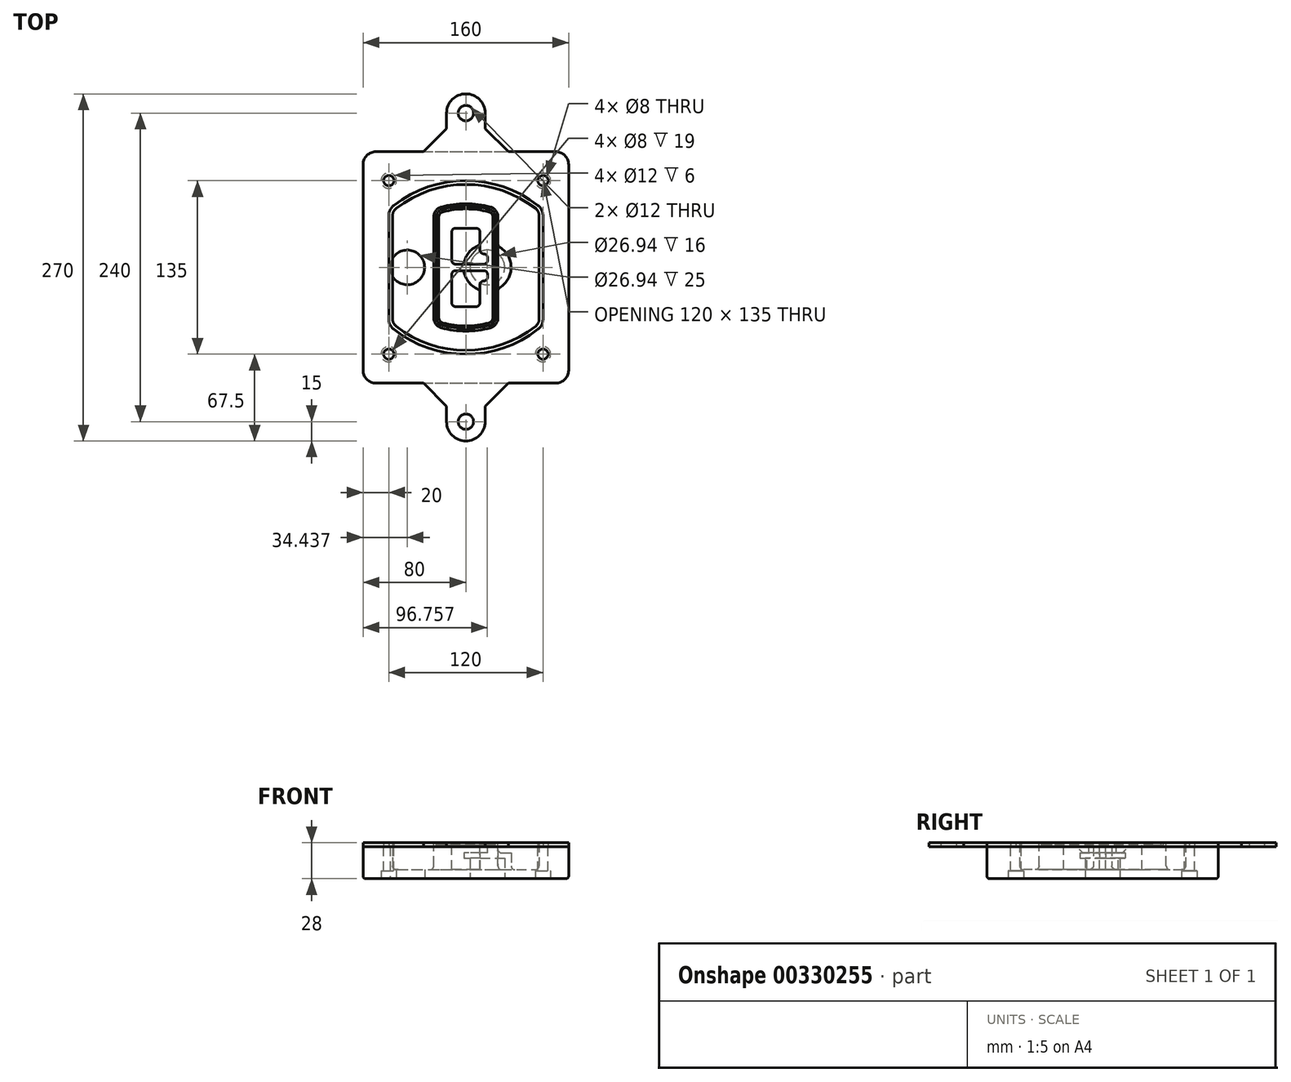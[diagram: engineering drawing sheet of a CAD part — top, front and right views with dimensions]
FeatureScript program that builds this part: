
annotation { "Feature Type Name" : "Feature", "Feature Type Description" : "" }
export const myFeature = defineFeature(function(context is Context, id is Id, definition is map)
    precondition{}
    {
        {
            var Q0;
            Q0=qCreatedBy(makeId("Top.planeOp"),FACE);
            var sketch = newSketch(context, id + "F0", { "sketchPlane" : qUnion([Q0])});
            skPoint(sketch, "E0.rect.middle", {"position": v(0, 0) * mm});
            skLineSegment(sketch, "E1.bottom", {"start": v(-70, -90) * mm, "end": v(70, -90) * mm});
            skLineSegment(sketch, "E1.top", {"start": v(-70, 90) * mm, "end": v(70, 90) * mm});
            skLineSegment(sketch, "E1.left", {"start": v(-80, -80) * mm, "end": v(-80, 80) * mm});
            skLineSegment(sketch, "E1.right", {"start": v(80, -80) * mm, "end": v(80, 80) * mm});
            skLineSegment(sketch, "E2", {"start": v(-80, 90) * mm, "end": v(80, -90) * mm, "construction": true});
            skLineSegment(sketch, "E3", {"start": v(80, 90) * mm, "end": v(-80, -90) * mm, "construction": true});
            skCircle(sketch, "E4", {"center": v(-60, 67.5) * mm, "radius": 4 * mm});
            skCircle(sketch, "E5", {"center": v(60, 67.5) * mm, "radius": 4 * mm});
            skCircle(sketch, "E6", {"center": v(60, -67.5) * mm, "radius": 4 * mm});
            skCircle(sketch, "E7", {"center": v(-60, -67.5) * mm, "radius": 4 * mm});
            skLineSegment(sketch, "E8", {"start": v(-60, 67.5) * mm, "end": v(60, 67.5) * mm, "construction": true});
            skLineSegment(sketch, "E9", {"start": v(60, 67.5) * mm, "end": v(60, -67.5) * mm, "construction": true});
            skLineSegment(sketch, "E10", {"start": v(60, -67.5) * mm, "end": v(-60, -67.5) * mm, "construction": true});
            skLineSegment(sketch, "E11", {"start": v(-60, -67.5) * mm, "end": v(-60, 67.5) * mm, "construction": true});
            skLineSegment(sketch, "E12", {"start": v(-60, 40.3) * mm, "end": v(-60, -40.3) * mm});
            skLineSegment(sketch, "E13", {"start": v(60, 40.3) * mm, "end": v(60, -40.3) * mm});
            skArc(sketch, "E14", {"start": v(56.15, 48.18) * mm, "mid": v(0, 67.5) * mm, "end": v(-56.15, 48.18) * mm});
            skArc(sketch, "E15", {"start": v(-56.15, -48.18) * mm, "mid": v(0, -67.5) * mm, "end": v(56.15, -48.18) * mm});
            skLineSegment(sketch, "E16", {"start": v(-60, 0) * mm, "end": v(60, 0) * mm, "construction": true});
            skPoint(sketch, "E17.visualSharp", {"position": v(-60, -45) * mm});
            skArc(sketch, "E17.filletArc", {"start": v(-60, -40.3) * mm, "mid": v(-58.99, -44.68) * mm, "end": v(-56.15, -48.18) * mm});
            skPoint(sketch, "E18.visualSharp", {"position": v(-60, 45) * mm});
            skArc(sketch, "E18.filletArc", {"start": v(-56.15, 48.18) * mm, "mid": v(-58.99, 44.68) * mm, "end": v(-60, 40.3) * mm});
            skPoint(sketch, "E19.visualSharp", {"position": v(60, 45) * mm});
            skArc(sketch, "E19.filletArc", {"start": v(60, 40.3) * mm, "mid": v(58.99, 44.68) * mm, "end": v(56.15, 48.18) * mm});
            skPoint(sketch, "E20.visualSharp", {"position": v(60, -45) * mm});
            skArc(sketch, "E20.filletArc", {"start": v(56.15, -48.18) * mm, "mid": v(58.99, -44.68) * mm, "end": v(60, -40.3) * mm});
            skPoint(sketch, "E21.visualSharp", {"position": v(-80, 90) * mm});
            skArc(sketch, "E21.filletArc", {"start": v(-70, 90) * mm, "mid": v(-77.07, 87.07) * mm, "end": v(-80, 80) * mm});
            skPoint(sketch, "E22.visualSharp", {"position": v(80, 90) * mm});
            skArc(sketch, "E22.filletArc", {"start": v(80, 80) * mm, "mid": v(77.07, 87.07) * mm, "end": v(70, 90) * mm});
            skPoint(sketch, "E23.visualSharp", {"position": v(80, -90) * mm});
            skArc(sketch, "E23.filletArc", {"start": v(70, -90) * mm, "mid": v(77.07, -87.07) * mm, "end": v(80, -80) * mm});
            skPoint(sketch, "E24.visualSharp", {"position": v(-80, -90) * mm});
            skArc(sketch, "E24.filletArc", {"start": v(-80, -80) * mm, "mid": v(-77.07, -87.07) * mm, "end": v(-70, -90) * mm});
            skArc(sketch, "E25.0", {"start": v(57, 40.3) * mm, "mid": v(56.3, 43.36) * mm, "end": v(54.3, 45.81) * mm});
            skLineSegment(sketch, "E25.1", {"start": v(57, 40.3) * mm, "end": v(57, -40.3) * mm});
            skArc(sketch, "E25.2", {"start": v(54.3, -45.81) * mm, "mid": v(56.3, -43.36) * mm, "end": v(57, -40.3) * mm});
            skArc(sketch, "E25.3", {"start": v(-54.3, -45.81) * mm, "mid": v(0, -64.5) * mm, "end": v(54.3, -45.81) * mm});
            skArc(sketch, "E25.4", {"start": v(-57, -40.3) * mm, "mid": v(-56.3, -43.36) * mm, "end": v(-54.3, -45.81) * mm});
            skArc(sketch, "E25.5", {"start": v(54.3, 45.81) * mm, "mid": v(0, 64.5) * mm, "end": v(-54.3, 45.81) * mm});
            skLineSegment(sketch, "E25.6", {"start": v(-57, 40.3) * mm, "end": v(-57, -40.3) * mm});
            skArc(sketch, "E25.7", {"start": v(-54.3, 45.81) * mm, "mid": v(-56.3, 43.36) * mm, "end": v(-57, 40.3) * mm});
            skArc(sketch, "E26.0", {"start": v(-58.62, 51.33) * mm, "mid": v(-62.58, 46.43) * mm, "end": v(-64, 40.3) * mm});
            skArc(sketch, "E26.1", {"start": v(58.62, 51.33) * mm, "mid": v(0, 71.5) * mm, "end": v(-58.62, 51.33) * mm});
            skArc(sketch, "E26.2", {"start": v(64, 40.3) * mm, "mid": v(62.58, 46.43) * mm, "end": v(58.62, 51.33) * mm});
            skLineSegment(sketch, "E26.3", {"start": v(64, 40.3) * mm, "end": v(64, -40.3) * mm});
            skArc(sketch, "E26.4", {"start": v(58.62, -51.33) * mm, "mid": v(62.58, -46.43) * mm, "end": v(64, -40.3) * mm});
            skLineSegment(sketch, "E26.5", {"start": v(-64, 40.3) * mm, "end": v(-64, -40.3) * mm});
            skArc(sketch, "E26.6", {"start": v(-58.62, -51.33) * mm, "mid": v(0, -71.5) * mm, "end": v(58.62, -51.33) * mm});
            skArc(sketch, "E26.7", {"start": v(-64, -40.3) * mm, "mid": v(-62.58, -46.43) * mm, "end": v(-58.62, -51.33) * mm});
            skSolve(sketch);
        }
        {
            var Q0;
            Q0=makeQuery(id+"F0.imprint","IMPRINT",FACE,{"disambiguationData":[TD([[makeQuery(id+"F0.imprint","IMPRINT",EDGE,{"derivedFrom":sQuery(id+"F0.wireOp",EDGE,"E1.bottom")}),1.0]])]});
            var Q1;
            Q1=makeQuery(id+"F0.imprint","IMPRINT",FACE,{"disambiguationData":[TD([[makeQuery(id+"F0.imprint","IMPRINT",EDGE,{"derivedFrom":sQuery(id+"F0.wireOp",EDGE,"E12")}),1.0]])]});
            var Q2;
            Q2=makeQuery(id+"F0.imprint","IMPRINT",FACE,{"disambiguationData":[TD([[makeQuery(id+"F0.imprint","IMPRINT",EDGE,{"derivedFrom":sQuery(id+"F0.wireOp",EDGE,"E25.0")}),1.0]])]});
            var Q3;
            Q3=makeQuery(id+"F0.imprint","IMPRINT",FACE,{"disambiguationData":[TD([[makeQuery(id+"F0.imprint","IMPRINT",EDGE,{"derivedFrom":sQuery(id+"F0.wireOp",EDGE,"E12")}),-1.0]])]});
            extrude(context, id + "F1", {"entities" : qUnion([Q0, Q1, Q2, Q3]), "oppositeDirection" : true, "depth" : 25 * mm});
        }
        {
            var Q0;
            Q0=makeQuery(id+"F0.imprint","IMPRINT",FACE,{"disambiguationData":[TD([[makeQuery(id+"F0.imprint","IMPRINT",EDGE,{"derivedFrom":sQuery(id+"F0.wireOp",EDGE,"E12")}),1.0]])]});
            extrude(context, id + "F2", {"entities" : qUnion([Q0]), "operationType" : NewBodyOperationType.ADD, "depth" : 3 * mm});
        }
        {
            var Q0;
            Q0=makeQuery(id+"F0.imprint","IMPRINT",FACE,{"disambiguationData":[TD([[makeQuery(id+"F0.imprint","IMPRINT",EDGE,{"derivedFrom":sQuery(id+"F0.wireOp",EDGE,"E25.0")}),1.0]])]});
            extrude(context, id + "F3", {"entities" : qUnion([Q0]), "operationType" : NewBodyOperationType.REMOVE, "oppositeDirection" : true, "depth" : 18 * mm});
        }
        {
            var Q0;
            Q0=makeQuery(id+"F2.opExtrude","CAP_FACE",FACE,{"disambiguationData":[OSD([sQuery(id+"F0.wireOp",EDGE,"E12"),sQuery(id+"F0.wireOp",EDGE,"E13"),sQuery(id+"F0.wireOp",EDGE,"E14"),sQuery(id+"F0.wireOp",EDGE,"E15"),sQuery(id+"F0.wireOp",EDGE,"E17.filletArc"),sQuery(id+"F0.wireOp",EDGE,"E18.filletArc"),sQuery(id+"F0.wireOp",EDGE,"E19.filletArc"),sQuery(id+"F0.wireOp",EDGE,"E20.filletArc"),sQuery(id+"F0.wireOp",EDGE,"E25.0"),sQuery(id+"F0.wireOp",EDGE,"E25.1"),sQuery(id+"F0.wireOp",EDGE,"E25.2"),sQuery(id+"F0.wireOp",EDGE,"E25.3"),sQuery(id+"F0.wireOp",EDGE,"E25.4"),sQuery(id+"F0.wireOp",EDGE,"E25.5"),sQuery(id+"F0.wireOp",EDGE,"E25.6"),sQuery(id+"F0.wireOp",EDGE,"E25.7")])],"isStart":false});
            var sketch = newSketch(context, id + "F4", { "sketchPlane" : qUnion([Q0])});
            skArc(sketch, "E27.0", {"start": v(-19.08, -46.97) * mm, "mid": v(0, -49.5) * mm, "end": v(19.08, -46.97) * mm});
            skArc(sketch, "E28.0", {"start": v(19.08, 46.97) * mm, "mid": v(0, 49.5) * mm, "end": v(-19.08, 46.97) * mm});
            skLineSegment(sketch, "E29", {"start": v(-25, 39.25) * mm, "end": v(-25, -39.25) * mm});
            skLineSegment(sketch, "E30", {"start": v(25, 39.25) * mm, "end": v(25, -39.25) * mm});
            skLineSegment(sketch, "E31", {"start": v(-25, 45.1) * mm, "end": v(25, 45.1) * mm, "construction": true});
            skLineSegment(sketch, "E32", {"start": v(-25, -45.1) * mm, "end": v(25, -45.1) * mm, "construction": true});
            skPoint(sketch, "E33.visualSharp", {"position": v(-25, 45.1) * mm});
            skArc(sketch, "E33.filletArc", {"start": v(-19.08, 46.97) * mm, "mid": v(-23.35, 44.11) * mm, "end": v(-25, 39.25) * mm});
            skPoint(sketch, "E34.visualSharp", {"position": v(25, 45.1) * mm});
            skArc(sketch, "E34.filletArc", {"start": v(25, 39.25) * mm, "mid": v(23.35, 44.11) * mm, "end": v(19.08, 46.97) * mm});
            skPoint(sketch, "E35.visualSharp", {"position": v(25, -45.1) * mm});
            skArc(sketch, "E35.filletArc", {"start": v(19.08, -46.97) * mm, "mid": v(23.35, -44.11) * mm, "end": v(25, -39.25) * mm});
            skPoint(sketch, "E36.visualSharp", {"position": v(-25, -45.1) * mm});
            skArc(sketch, "E36.filletArc", {"start": v(-25, -39.25) * mm, "mid": v(-23.35, -44.11) * mm, "end": v(-19.08, -46.97) * mm});
            skArc(sketch, "E37.0", {"start": v(54.3, 45.81) * mm, "mid": v(0, 64.5) * mm, "end": v(-54.3, 45.81) * mm});
            skArc(sketch, "E37.1", {"start": v(-54.3, 45.81) * mm, "mid": v(-56.3, 43.36) * mm, "end": v(-57, 40.3) * mm});
            skLineSegment(sketch, "E37.2", {"start": v(-57, 40.3) * mm, "end": v(-57, -40.3) * mm});
            skArc(sketch, "E37.3", {"start": v(-57, -40.3) * mm, "mid": v(-56.3, -43.36) * mm, "end": v(-54.3, -45.81) * mm});
            skArc(sketch, "E37.4", {"start": v(-54.3, -45.81) * mm, "mid": v(0, -64.5) * mm, "end": v(54.3, -45.81) * mm});
            skArc(sketch, "E37.5", {"start": v(54.3, -45.81) * mm, "mid": v(56.3, -43.36) * mm, "end": v(57, -40.3) * mm});
            skLineSegment(sketch, "E37.6", {"start": v(57, 40.3) * mm, "end": v(57, -40.3) * mm});
            skArc(sketch, "E37.7", {"start": v(57, 40.3) * mm, "mid": v(56.3, 43.36) * mm, "end": v(54.3, 45.81) * mm});
            skLineSegment(sketch, "E38.0", {"start": v(23, 39.25) * mm, "end": v(23, -39.25) * mm});
            skArc(sketch, "E38.1", {"start": v(18.56, -45.04) * mm, "mid": v(21.76, -42.9) * mm, "end": v(23, -39.25) * mm});
            skArc(sketch, "E38.2", {"start": v(-18.56, -45.04) * mm, "mid": v(0, -47.5) * mm, "end": v(18.56, -45.04) * mm});
            skArc(sketch, "E38.3", {"start": v(-23, -39.25) * mm, "mid": v(-21.76, -42.9) * mm, "end": v(-18.56, -45.04) * mm});
            skLineSegment(sketch, "E38.4", {"start": v(-23, 39.25) * mm, "end": v(-23, -39.25) * mm});
            skArc(sketch, "E38.5", {"start": v(23, 39.25) * mm, "mid": v(21.76, 42.9) * mm, "end": v(18.56, 45.04) * mm});
            skArc(sketch, "E38.6", {"start": v(-18.56, 45.04) * mm, "mid": v(-21.76, 42.9) * mm, "end": v(-23, 39.25) * mm});
            skArc(sketch, "E38.7", {"start": v(18.56, 45.04) * mm, "mid": v(0, 47.5) * mm, "end": v(-18.56, 45.04) * mm});
            skArc(sketch, "E39.0", {"start": v(21, 39.25) * mm, "mid": v(20.18, 41.68) * mm, "end": v(18.04, 43.1) * mm});
            skLineSegment(sketch, "E39.1", {"start": v(21, 39.25) * mm, "end": v(21, -39.25) * mm});
            skArc(sketch, "E39.2", {"start": v(18.04, -43.1) * mm, "mid": v(20.18, -41.68) * mm, "end": v(21, -39.25) * mm});
            skArc(sketch, "E39.3", {"start": v(-18.04, -43.1) * mm, "mid": v(0, -45.5) * mm, "end": v(18.04, -43.1) * mm});
            skArc(sketch, "E39.4", {"start": v(-21, -39.25) * mm, "mid": v(-20.18, -41.68) * mm, "end": v(-18.04, -43.1) * mm});
            skArc(sketch, "E39.5", {"start": v(18.04, 43.1) * mm, "mid": v(0, 45.5) * mm, "end": v(-18.04, 43.1) * mm});
            skLineSegment(sketch, "E39.6", {"start": v(-21, 39.25) * mm, "end": v(-21, -39.25) * mm});
            skArc(sketch, "E39.7", {"start": v(-18.04, 43.1) * mm, "mid": v(-20.18, 41.68) * mm, "end": v(-21, 39.25) * mm});
            skLineSegment(sketch, "E40", {"start": v(-25, 0) * mm, "end": v(25, 0) * mm, "construction": true});
            skLineSegment(sketch, "E41", {"start": v(-11, 5.5) * mm, "end": v(-11, 27.5) * mm});
            skLineSegment(sketch, "E42", {"start": v(-8, 30.5) * mm, "end": v(8, 30.5) * mm});
            skLineSegment(sketch, "E43", {"start": v(11, 27.5) * mm, "end": v(11, 13.5) * mm});
            skLineSegment(sketch, "E44", {"start": v(14, 10.5) * mm, "end": v(14, 10.5) * mm});
            skLineSegment(sketch, "E45", {"start": v(17, 7.5) * mm, "end": v(17, 5.5) * mm});
            skLineSegment(sketch, "E46", {"start": v(14, 2.5) * mm, "end": v(-8, 2.5) * mm});
            skPoint(sketch, "E47.visualSharp", {"position": v(-11, 30.5) * mm});
            skArc(sketch, "E47.filletArc", {"start": v(-8, 30.5) * mm, "mid": v(-10.12, 29.62) * mm, "end": v(-11, 27.5) * mm});
            skPoint(sketch, "E48.visualSharp", {"position": v(11, 30.5) * mm});
            skArc(sketch, "E48.filletArc", {"start": v(11, 27.5) * mm, "mid": v(10.12, 29.62) * mm, "end": v(8, 30.5) * mm});
            skPoint(sketch, "E49.visualSharp", {"position": v(11, 10.5) * mm});
            skArc(sketch, "E49.filletArc", {"start": v(11, 13.5) * mm, "mid": v(11.88, 11.38) * mm, "end": v(14, 10.5) * mm});
            skPoint(sketch, "E50.visualSharp", {"position": v(17, 10.5) * mm});
            skArc(sketch, "E50.filletArc", {"start": v(17, 7.5) * mm, "mid": v(16.12, 9.62) * mm, "end": v(14, 10.5) * mm});
            skPoint(sketch, "E51.visualSharp", {"position": v(17, 2.5) * mm});
            skArc(sketch, "E51.filletArc", {"start": v(14, 2.5) * mm, "mid": v(16.12, 3.38) * mm, "end": v(17, 5.5) * mm});
            skPoint(sketch, "E52.visualSharp", {"position": v(-11, 2.5) * mm});
            skArc(sketch, "E52.filletArc", {"start": v(-11, 5.5) * mm, "mid": v(-10.12, 3.38) * mm, "end": v(-8, 2.5) * mm});
            skLineSegment(sketch, "E53.0.MirrorCS", {"start": v(14, -2.5) * mm, "end": v(-8, -2.5) * mm});
            skArc(sketch, "E54.0.MirrorCS", {"start": v(-11, -5.5) * mm, "mid": v(-10.12, -3.38) * mm, "end": v(-8, -2.5) * mm});
            skLineSegment(sketch, "E55.0.MirrorCS", {"start": v(-11, -5.5) * mm, "end": v(-11, -27.5) * mm});
            skArc(sketch, "E56.0.MirrorCS", {"start": v(-8, -30.5) * mm, "mid": v(-10.12, -29.62) * mm, "end": v(-11, -27.5) * mm});
            skLineSegment(sketch, "E57.0.MirrorCS", {"start": v(-8, -30.5) * mm, "end": v(8, -30.5) * mm});
            skArc(sketch, "E58.0.MirrorCS", {"start": v(11, -27.5) * mm, "mid": v(10.12, -29.62) * mm, "end": v(8, -30.5) * mm});
            skLineSegment(sketch, "E59.0.MirrorCS", {"start": v(11, -27.5) * mm, "end": v(11, -13.5) * mm});
            skArc(sketch, "E60.0.MirrorCS", {"start": v(11, -13.5) * mm, "mid": v(11.88, -11.38) * mm, "end": v(14, -10.5) * mm});
            skArc(sketch, "E61.0.MirrorCS", {"start": v(17, -7.5) * mm, "mid": v(16.12, -9.62) * mm, "end": v(14, -10.5) * mm});
            skLineSegment(sketch, "E62.0.MirrorCS", {"start": v(17, -7.5) * mm, "end": v(17, -5.5) * mm});
            skArc(sketch, "E63.0.MirrorCS", {"start": v(14, -2.5) * mm, "mid": v(16.12, -3.38) * mm, "end": v(17, -5.5) * mm});
            skSolve(sketch);
        }
        {
            var Q0;
            Q0=makeQuery(id+"F4.imprint","IMPRINT",FACE,{"disambiguationData":[TD([[makeQuery(id+"F4.imprint","IMPRINT",EDGE,{"derivedFrom":sQuery(id+"F4.wireOp",EDGE,"E27.0")}),1.0]])]});
            var Q1;
            Q1=makeQuery(id+"F4.imprint","IMPRINT",FACE,{"disambiguationData":[TD([[makeQuery(id+"F4.imprint","IMPRINT",EDGE,{"derivedFrom":sQuery(id+"F4.wireOp",EDGE,"E38.0")}),-1.0]])]});
            var Q2;
            Q2=makeQuery(id+"F4.imprint","IMPRINT",FACE,{"disambiguationData":[TD([[makeQuery(id+"F4.imprint","IMPRINT",EDGE,{"derivedFrom":sQuery(id+"F4.wireOp",EDGE,"E39.0")}),1.0]])]});
            extrude(context, id + "F5", {"entities" : qUnion([Q0, Q1, Q2]), "operationType" : NewBodyOperationType.ADD, "endBound" : BoundingType.UP_TO_NEXT, "oppositeDirection" : true, "depth" : 25 * mm});
        }
        {
            var Q0;
            Q0=makeQuery(id+"F4.imprint","IMPRINT",FACE,{"disambiguationData":[TD([[makeQuery(id+"F4.imprint","IMPRINT",EDGE,{"derivedFrom":sQuery(id+"F4.wireOp",EDGE,"E38.0")}),-1.0]])]});
            extrude(context, id + "F6", {"entities" : qUnion([Q0]), "operationType" : NewBodyOperationType.REMOVE, "oppositeDirection" : true, "depth" : 2 * mm});
        }
        {
            var Q0;
            Q0=makeQuery(id+"F1.opExtrude","CAP_FACE",FACE,{"disambiguationData":[OSD([sQuery(id+"F0.wireOp",EDGE,"E1.bottom"),sQuery(id+"F0.wireOp",EDGE,"E1.top"),sQuery(id+"F0.wireOp",EDGE,"E1.left"),sQuery(id+"F0.wireOp",EDGE,"E1.right"),sQuery(id+"F0.wireOp",EDGE,"E4"),sQuery(id+"F0.wireOp",EDGE,"E5"),sQuery(id+"F0.wireOp",EDGE,"E6"),sQuery(id+"F0.wireOp",EDGE,"E7"),sQuery(id+"F0.wireOp",EDGE,"E21.filletArc"),sQuery(id+"F0.wireOp",EDGE,"E22.filletArc"),sQuery(id+"F0.wireOp",EDGE,"E23.filletArc"),sQuery(id+"F0.wireOp",EDGE,"E24.filletArc")])],"isStart":false});
            var sketch = newSketch(context, id + "F7", { "sketchPlane" : qUnion([Q0])});
            skCircle(sketch, "E64", {"center": v(16.76, 0) * mm, "radius": 13.47 * mm});
            skCircle(sketch, "E65", {"center": v(-45.56, 0) * mm, "radius": 13.47 * mm});
            skLineSegment(sketch, "E66", {"start": v(80, 0) * mm, "end": v(-80, 0) * mm});
            skCircle(sketch, "E67", {"center": v(16.76, 0) * mm, "radius": 18.47 * mm});
            skCircle(sketch, "E68", {"center": v(60, -67.5) * mm, "radius": 6 * mm});
            skCircle(sketch, "E69", {"center": v(-60, -67.5) * mm, "radius": 6 * mm});
            skCircle(sketch, "E70", {"center": v(-60, 67.5) * mm, "radius": 6 * mm});
            skCircle(sketch, "E71", {"center": v(60, 67.5) * mm, "radius": 6 * mm});
            skSolve(sketch);
        }
        {
            var Q0;
            {var subQ1=sQuery(id+"F7.wireOp",EDGE,"E66");var subQ4=sQuery(id+"F7.wireOp",EDGE,"E64");var subQ6=makeQuery(id+"F7.imprint","INTERSECT",VERTEX,{"disambiguationData":[OD(0.0)],"derivedFrom":[subQ4,subQ1]});Q0=makeQuery(id+"F7.imprint","IMPRINT",FACE,{"disambiguationData":[TD([[makeQuery(id+"F7.imprint","IMPRINT",EDGE,{"disambiguationData":[TD([[subQ6,-1.0]])],"derivedFrom":subQ4}),-1.0]])]});}
            var Q1;
            {var subQ0=sQuery(id+"F7.wireOp",EDGE,"E66");var subQ1=sQuery(id+"F7.wireOp",EDGE,"E64");var subQ3=makeQuery(id+"F7.imprint","INTERSECT",VERTEX,{"disambiguationData":[OD(0.0)],"derivedFrom":[subQ1,subQ0]});Q1=makeQuery(id+"F7.imprint","IMPRINT",FACE,{"disambiguationData":[TD([[makeQuery(id+"F7.imprint","IMPRINT",EDGE,{"disambiguationData":[TD([[subQ3,-1.0]])],"derivedFrom":subQ1}),1.0]])]});}
            var Q2;
            {var subQ0=sQuery(id+"F7.wireOp",EDGE,"E66");var subQ1=sQuery(id+"F7.wireOp",EDGE,"E64");var subQ3=makeQuery(id+"F7.imprint","INTERSECT",VERTEX,{"disambiguationData":[OD(0.0)],"derivedFrom":[subQ1,subQ0]});Q2=makeQuery(id+"F7.imprint","IMPRINT",FACE,{"disambiguationData":[TD([[makeQuery(id+"F7.imprint","IMPRINT",EDGE,{"disambiguationData":[TD([[subQ3,1.0]])],"derivedFrom":subQ1}),1.0]])]});}
            var Q3;
            {var subQ1=sQuery(id+"F7.wireOp",EDGE,"E66");var subQ4=sQuery(id+"F7.wireOp",EDGE,"E64");var subQ6=makeQuery(id+"F7.imprint","INTERSECT",VERTEX,{"disambiguationData":[OD(0.0)],"derivedFrom":[subQ4,subQ1]});Q3=makeQuery(id+"F7.imprint","IMPRINT",FACE,{"disambiguationData":[TD([[makeQuery(id+"F7.imprint","IMPRINT",EDGE,{"disambiguationData":[TD([[subQ6,1.0]])],"derivedFrom":subQ4}),-1.0]])]});}
            extrude(context, id + "F8", {"entities" : qUnion([Q0, Q1, Q2, Q3]), "operationType" : NewBodyOperationType.ADD, "oppositeDirection" : true, "depth" : 20 * mm});
        }
        {
            var Q0;
            {var subQ0=sQuery(id+"F7.wireOp",EDGE,"E66");var subQ1=sQuery(id+"F7.wireOp",EDGE,"E64");var subQ3=makeQuery(id+"F7.imprint","INTERSECT",VERTEX,{"disambiguationData":[OD(0.0)],"derivedFrom":[subQ1,subQ0]});Q0=makeQuery(id+"F7.imprint","IMPRINT",FACE,{"disambiguationData":[TD([[makeQuery(id+"F7.imprint","IMPRINT",EDGE,{"disambiguationData":[TD([[subQ3,-1.0]])],"derivedFrom":subQ1}),1.0]])]});}
            var Q1;
            {var subQ0=sQuery(id+"F7.wireOp",EDGE,"E66");var subQ1=sQuery(id+"F7.wireOp",EDGE,"E64");var subQ3=makeQuery(id+"F7.imprint","INTERSECT",VERTEX,{"disambiguationData":[OD(0.0)],"derivedFrom":[subQ1,subQ0]});Q1=makeQuery(id+"F7.imprint","IMPRINT",FACE,{"disambiguationData":[TD([[makeQuery(id+"F7.imprint","IMPRINT",EDGE,{"disambiguationData":[TD([[subQ3,1.0]])],"derivedFrom":subQ1}),1.0]])]});}
            extrude(context, id + "F9", {"entities" : qUnion([Q0, Q1]), "operationType" : NewBodyOperationType.REMOVE, "oppositeDirection" : true, "depth" : 16 * mm});
        }
        {
            var Q0;
            {var subQ0=sQuery(id+"F7.wireOp",EDGE,"E66");var subQ1=sQuery(id+"F7.wireOp",EDGE,"E65");var subQ3=makeQuery(id+"F7.imprint","INTERSECT",VERTEX,{"disambiguationData":[OD(0.0)],"derivedFrom":[subQ1,subQ0]});Q0=makeQuery(id+"F7.imprint","IMPRINT",FACE,{"disambiguationData":[TD([[makeQuery(id+"F7.imprint","IMPRINT",EDGE,{"disambiguationData":[TD([[subQ3,-1.0]])],"derivedFrom":subQ1}),1.0]])]});}
            var Q1;
            {var subQ0=sQuery(id+"F7.wireOp",EDGE,"E66");var subQ1=sQuery(id+"F7.wireOp",EDGE,"E65");var subQ3=makeQuery(id+"F7.imprint","INTERSECT",VERTEX,{"disambiguationData":[OD(0.0)],"derivedFrom":[subQ1,subQ0]});Q1=makeQuery(id+"F7.imprint","IMPRINT",FACE,{"disambiguationData":[TD([[makeQuery(id+"F7.imprint","IMPRINT",EDGE,{"disambiguationData":[TD([[subQ3,1.0]])],"derivedFrom":subQ1}),1.0]])]});}
            extrude(context, id + "F10", {"entities" : qUnion([Q0, Q1]), "operationType" : NewBodyOperationType.REMOVE, "oppositeDirection" : true, "depth" : 25 * mm});
        }
        {
            var Q0;
            Q0=makeQuery(id+"F7.imprint","IMPRINT",FACE,{"disambiguationData":[TD([[makeQuery(id+"F7.imprint","IMPRINT",EDGE,{"derivedFrom":sQuery(id+"F7.wireOp",EDGE,"E68")}),1.0]])]});
            var Q1;
            Q1=makeQuery(id+"F7.imprint","IMPRINT",FACE,{"disambiguationData":[TD([[makeQuery(id+"F7.imprint","IMPRINT",EDGE,{"derivedFrom":makeQuery(id+"F1.opExtrude","CAP_EDGE",EDGE,{"disambiguationData":[OSD([sQuery(id+"F0.wireOp",EDGE,"E5")])],"isStart":false})}),-1.0]])]});
            var Q2;
            Q2=makeQuery(id+"F7.imprint","IMPRINT",FACE,{"disambiguationData":[TD([[makeQuery(id+"F7.imprint","IMPRINT",EDGE,{"derivedFrom":sQuery(id+"F7.wireOp",EDGE,"E69")}),1.0]])]});
            var Q3;
            Q3=makeQuery(id+"F7.imprint","IMPRINT",FACE,{"disambiguationData":[TD([[makeQuery(id+"F7.imprint","IMPRINT",EDGE,{"derivedFrom":makeQuery(id+"F1.opExtrude","CAP_EDGE",EDGE,{"disambiguationData":[OSD([sQuery(id+"F0.wireOp",EDGE,"E4")])],"isStart":false})}),-1.0]])]});
            var Q4;
            Q4=makeQuery(id+"F7.imprint","IMPRINT",FACE,{"disambiguationData":[TD([[makeQuery(id+"F7.imprint","IMPRINT",EDGE,{"derivedFrom":sQuery(id+"F7.wireOp",EDGE,"E70")}),1.0]])]});
            var Q5;
            Q5=makeQuery(id+"F7.imprint","IMPRINT",FACE,{"disambiguationData":[TD([[makeQuery(id+"F7.imprint","IMPRINT",EDGE,{"derivedFrom":makeQuery(id+"F1.opExtrude","CAP_EDGE",EDGE,{"disambiguationData":[OSD([sQuery(id+"F0.wireOp",EDGE,"E7")])],"isStart":false})}),-1.0]])]});
            var Q6;
            Q6=makeQuery(id+"F7.imprint","IMPRINT",FACE,{"disambiguationData":[TD([[makeQuery(id+"F7.imprint","IMPRINT",EDGE,{"derivedFrom":sQuery(id+"F7.wireOp",EDGE,"E71")}),1.0]])]});
            var Q7;
            Q7=makeQuery(id+"F7.imprint","IMPRINT",FACE,{"disambiguationData":[TD([[makeQuery(id+"F7.imprint","IMPRINT",EDGE,{"derivedFrom":makeQuery(id+"F1.opExtrude","CAP_EDGE",EDGE,{"disambiguationData":[OSD([sQuery(id+"F0.wireOp",EDGE,"E6")])],"isStart":false})}),-1.0]])]});
            extrude(context, id + "F11", {"entities" : qUnion([Q0, Q1, Q2, Q3, Q4, Q5, Q6, Q7]), "operationType" : NewBodyOperationType.REMOVE, "oppositeDirection" : true, "depth" : 6 * mm});
        }
        {
            var Q0;
            Q0=makeQuery(id+"F9.boolean.opBoolean","COPY",FACE,{"derivedFrom":makeQuery(id+"F9.opExtrude","CAP_FACE",FACE,{"disambiguationData":[OSD([sQuery(id+"F7.wireOp",EDGE,"E64")])],"isStart":false})});
            var sketch = newSketch(context, id + "F12", { "sketchPlane" : qUnion([Q0])});
            skArc(sketch, "E72.0", {"start": v(11, 17.55) * mm, "mid": v(2.57, 11.82) * mm, "end": v(-1.54, 2.5) * mm});
            skArc(sketch, "E72.1", {"start": v(-1.54, -2.5) * mm, "mid": v(2.57, -11.82) * mm, "end": v(11, -17.55) * mm});
            skLineSegment(sketch, "E73", {"start": v(-1.54, -2.5) * mm, "end": v(14, -2.5) * mm});
            skLineSegment(sketch, "E74.0", {"start": v(14, 2.5) * mm, "end": v(-1.54, 2.5) * mm});
            skArc(sketch, "E74.1", {"start": v(14, 2.5) * mm, "mid": v(16.12, 3.38) * mm, "end": v(17, 5.5) * mm});
            skLineSegment(sketch, "E74.2", {"start": v(17, 7.5) * mm, "end": v(17, 5.5) * mm});
            skArc(sketch, "E74.3", {"start": v(17, 7.5) * mm, "mid": v(16.12, 9.62) * mm, "end": v(14, 10.5) * mm});
            skArc(sketch, "E74.4", {"start": v(11, 13.5) * mm, "mid": v(11.88, 11.38) * mm, "end": v(14, 10.5) * mm});
            skLineSegment(sketch, "E74.5", {"start": v(11, 17.55) * mm, "end": v(11, 13.5) * mm});
            skLineSegment(sketch, "E74.7", {"start": v(14, -2.5) * mm, "end": v(-1.54, -2.5) * mm});
            skArc(sketch, "E74.8", {"start": v(14, -2.5) * mm, "mid": v(16.12, -3.38) * mm, "end": v(17, -5.5) * mm});
            skLineSegment(sketch, "E74.9", {"start": v(17, -7.5) * mm, "end": v(17, -5.5) * mm});
            skArc(sketch, "E74.10", {"start": v(17, -7.5) * mm, "mid": v(16.12, -9.62) * mm, "end": v(14, -10.5) * mm});
            skArc(sketch, "E74.11", {"start": v(11, -13.5) * mm, "mid": v(11.88, -11.38) * mm, "end": v(14, -10.5) * mm});
            skLineSegment(sketch, "E74.12", {"start": v(11, -17.55) * mm, "end": v(11, -13.5) * mm});
            skPoint(sketch, "E75.orphan", {"position": v(11, -27.5) * mm});
            skPoint(sketch, "E76.orphan", {"position": v(-8, -2.5) * mm});
            skPoint(sketch, "E77.orphan", {"position": v(-8, 2.5) * mm});
            skPoint(sketch, "E78.orphan", {"position": v(11, 27.5) * mm});
            skSolve(sketch);
        }
        {
            var Q0;
            {var subQ7=sQuery(id+"F12.wireOp",EDGE,"E72.0");var subQ14=sQuery(id+"F12.wireOp",EDGE,"E72.1");var subQ16=sQuery(id+"F12.wireOp",EDGE,"E74.1");var subQ18=sQuery(id+"F12.wireOp",EDGE,"E74.8");Q0=qUnion([makeQuery(id+"F12.imprint","IMPRINT",FACE,{"disambiguationData":[TD([[makeQuery(id+"F12.imprint","IMPRINT",EDGE,{"derivedFrom":subQ7}),1.0]])]}),makeQuery(id+"F12.imprint","IMPRINT",FACE,{"disambiguationData":[TD([[makeQuery(id+"F12.imprint","IMPRINT",EDGE,{"derivedFrom":subQ14}),1.0]])]}),makeQuery(id+"F12.imprint","IMPRINT",FACE,{"disambiguationData":[TD([[makeQuery(id+"F12.imprint","IMPRINT",EDGE,{"derivedFrom":subQ16}),1.0]])]}),makeQuery(id+"F12.imprint","IMPRINT",FACE,{"disambiguationData":[TD([[makeQuery(id+"F12.imprint","IMPRINT",EDGE,{"derivedFrom":subQ18}),-1.0]])]})]);}
            var Q1;
            Q1=makeQuery(id+"F5.boolean.opBoolean","SPLIT",FACE,{"disambiguationData":[TD([makeQuery(id+"F5.opExtrude","SWEPT_FACE",FACE,{"disambiguationData":[OSD([sQuery(id+"F4.wireOp",EDGE,"E41")])]})])],"derivedFrom":makeQuery(id+"F3.boolean.opBoolean","COPY",FACE,{"derivedFrom":makeQuery(id+"F3.opExtrude","CAP_FACE",FACE,{"disambiguationData":[OSD([sQuery(id+"F0.wireOp",EDGE,"E25.0"),sQuery(id+"F0.wireOp",EDGE,"E25.1"),sQuery(id+"F0.wireOp",EDGE,"E25.2"),sQuery(id+"F0.wireOp",EDGE,"E25.3"),sQuery(id+"F0.wireOp",EDGE,"E25.4"),sQuery(id+"F0.wireOp",EDGE,"E25.5"),sQuery(id+"F0.wireOp",EDGE,"E25.6"),sQuery(id+"F0.wireOp",EDGE,"E25.7")])],"isStart":false})})});
            extrude(context, id + "F13", {"entities" : qUnion([Q0]), "operationType" : NewBodyOperationType.REMOVE, "endBound" : BoundingType.UP_TO_SURFACE, "endBoundEntityFace" : qUnion([Q1]), "depth" : 25 * mm});
        }
        {
            var Q0;
            Q0=makeQuery(id+"F3.boolean.opBoolean","COPY",EDGE,{"derivedFrom":makeQuery(id+"F3.opExtrude","CAP_EDGE",EDGE,{"disambiguationData":[OSD([sQuery(id+"F0.wireOp",EDGE,"E25.6")])],"isStart":false})});
            var Q1;
            Q1=makeQuery(id+"F8.boolean.opBoolean","INTERSECT",EDGE,{"derivedFrom":[makeQuery(id+"F5.opExtrude","SWEPT_FACE",FACE,{"disambiguationData":[OSD([sQuery(id+"F4.wireOp",EDGE,"E30")])]}),makeQuery(id+"F8.opExtrude","CAP_FACE",FACE,{"disambiguationData":[OSD([sQuery(id+"F7.wireOp",EDGE,"E67")])],"isStart":false})]});
            var Q2;
            Q2=makeQuery(id+"F8.boolean.opBoolean","INTERSECT",EDGE,{"disambiguationData":[OD(1.0)],"derivedFrom":[makeQuery(id+"F5.opExtrude","SWEPT_FACE",FACE,{"disambiguationData":[OSD([sQuery(id+"F4.wireOp",EDGE,"E30")])]}),makeQuery(id+"F8.opExtrude","SWEPT_FACE",FACE,{"disambiguationData":[OSD([sQuery(id+"F7.wireOp",EDGE,"E67")])]})]});
            var Q3;
            {var subQ0=sQuery(id+"F4.wireOp",EDGE,"E30");Q3=makeQuery(id+"F8.boolean.opBoolean","SPLIT",EDGE,{"disambiguationData":[TD([makeQuery(id+"F5.opExtrude","SWEPT_FACE",FACE,{"disambiguationData":[OSD([sQuery(id+"F4.wireOp",EDGE,"E35.filletArc")])]})])],"derivedFrom":makeQuery(id+"F5.opExtrude","CAP_EDGE",EDGE,{"disambiguationData":[OSD([subQ0])],"isStart":false})});}
            var Q4;
            {var subQ0=sQuery(id+"F0.wireOp",EDGE,"E25.7");var subQ1=sQuery(id+"F0.wireOp",EDGE,"E25.1");var subQ2=sQuery(id+"F0.wireOp",EDGE,"E25.6");var subQ3=sQuery(id+"F0.wireOp",EDGE,"E25.5");var subQ4=sQuery(id+"F0.wireOp",EDGE,"E25.4");var subQ5=sQuery(id+"F0.wireOp",EDGE,"E25.0");var subQ6=sQuery(id+"F0.wireOp",EDGE,"E25.2");var subQ7=sQuery(id+"F0.wireOp",EDGE,"E25.3");Q4=makeQuery(id+"F8.boolean.opBoolean","INTERSECT",EDGE,{"derivedFrom":[makeQuery(id+"F5.boolean.opBoolean","SPLIT",FACE,{"disambiguationData":[TD([makeQuery(id+"F2.opExtrude","SWEPT_FACE",FACE,{"disambiguationData":[OSD([subQ5])]})])],"derivedFrom":makeQuery(id+"F3.boolean.opBoolean","COPY",FACE,{"derivedFrom":makeQuery(id+"F3.opExtrude","CAP_FACE",FACE,{"disambiguationData":[OSD([subQ5,subQ1,subQ6,subQ7,subQ4,subQ3,subQ2,subQ0])],"isStart":false})})}),makeQuery(id+"F8.opExtrude","SWEPT_FACE",FACE,{"disambiguationData":[OSD([sQuery(id+"F7.wireOp",EDGE,"E67")])]})]});}
            var Q5;
            Q5=makeQuery(id+"F8.boolean.opBoolean","INTERSECT",EDGE,{"disambiguationData":[OD(0.0)],"derivedFrom":[makeQuery(id+"F5.opExtrude","SWEPT_FACE",FACE,{"disambiguationData":[OSD([sQuery(id+"F4.wireOp",EDGE,"E30")])]}),makeQuery(id+"F8.opExtrude","SWEPT_FACE",FACE,{"disambiguationData":[OSD([sQuery(id+"F7.wireOp",EDGE,"E67")])]})]});
            fillet(context, id + "F14", {"entities" : qUnion([Q0, Q1, Q2, Q3, Q4, Q5]), "radius" : 3 * mm, "tangentPropagation" : true, "allowEdgeOverflow" : false});
        }
        {
            var Q0;
            Q0=makeQuery(id+"F1.opExtrude","CAP_EDGE",EDGE,{"disambiguationData":[OSD([sQuery(id+"F0.wireOp",EDGE,"E1.bottom")])],"isStart":false});
            fillet(context, id + "F15", {"entities" : qUnion([Q0]), "radius" : 2 * mm, "tangentPropagation" : true, "allowEdgeOverflow" : false});
        }
        {
            var Q0;
            {var subQ0=sQuery(id+"F0.wireOp",EDGE,"E21.filletArc");var subQ1=sQuery(id+"F0.wireOp",EDGE,"E7");var subQ2=sQuery(id+"F0.wireOp",EDGE,"E6");var subQ3=sQuery(id+"F0.wireOp",EDGE,"E5");var subQ4=sQuery(id+"F0.wireOp",EDGE,"E4");var subQ5=sQuery(id+"F0.wireOp",EDGE,"E22.filletArc");var subQ6=sQuery(id+"F0.wireOp",EDGE,"E1.bottom");var subQ7=sQuery(id+"F0.wireOp",EDGE,"E1.right");var subQ8=sQuery(id+"F0.wireOp",EDGE,"E1.top");var subQ9=sQuery(id+"F0.wireOp",EDGE,"E1.left");var subQ10=sQuery(id+"F0.wireOp",EDGE,"E23.filletArc");var subQ11=sQuery(id+"F0.wireOp",EDGE,"E24.filletArc");Q0=makeQuery(id+"F2.boolean.opBoolean","SPLIT",FACE,{"disambiguationData":[TD([makeQuery(id+"F1.opExtrude","SWEPT_FACE",FACE,{"disambiguationData":[OSD([subQ6])]})])],"derivedFrom":makeQuery(id+"F1.opExtrude","CAP_FACE",FACE,{"disambiguationData":[OSD([subQ6,subQ8,subQ9,subQ7,subQ4,subQ3,subQ2,subQ1,subQ0,subQ5,subQ10,subQ11])],"isStart":true})});}
            var sketch = newSketch(context, id + "F16", { "sketchPlane" : qUnion([Q0])});
            skArc(sketch, "E79.0", {"start": v(-70, 90) * mm, "mid": v(-77.07, 87.07) * mm, "end": v(-80, 80) * mm});
            skLineSegment(sketch, "E80.0", {"start": v(-70, 90) * mm, "end": v(70, 90) * mm});
            skArc(sketch, "E81.2", {"start": v(80, 80) * mm, "mid": v(77.07, 87.07) * mm, "end": v(70, 90) * mm});
            skLineSegment(sketch, "E81.3", {"start": v(80, -80) * mm, "end": v(80, 80) * mm});
            skLineSegment(sketch, "E81.4", {"start": v(-80, -80) * mm, "end": v(-80, 80) * mm});
            skArc(sketch, "E81.5", {"start": v(-80, -80) * mm, "mid": v(-77.07, -87.07) * mm, "end": v(-70, -90) * mm});
            skLineSegment(sketch, "E81.6", {"start": v(-70, -90) * mm, "end": v(70, -90) * mm});
            skCircle(sketch, "E81.7", {"center": v(-60, 67.5) * mm, "radius": 4 * mm});
            skCircle(sketch, "E81.8", {"center": v(-60, -67.5) * mm, "radius": 4 * mm});
            skCircle(sketch, "E81.9", {"center": v(60, -67.5) * mm, "radius": 4 * mm});
            skCircle(sketch, "E81.10", {"center": v(60, 67.5) * mm, "radius": 4 * mm});
            skLineSegment(sketch, "E81.11", {"start": v(60, 40.3) * mm, "end": v(60, -40.3) * mm});
            skArc(sketch, "E81.12", {"start": v(56.15, 48.18) * mm, "mid": v(0, 67.5) * mm, "end": v(-56.15, 48.18) * mm});
            skArc(sketch, "E81.13", {"start": v(60, 40.3) * mm, "mid": v(58.99, 44.68) * mm, "end": v(56.15, 48.18) * mm});
            skArc(sketch, "E81.14", {"start": v(56.15, -48.18) * mm, "mid": v(58.99, -44.68) * mm, "end": v(60, -40.3) * mm});
            skArc(sketch, "E81.15", {"start": v(-56.15, -48.18) * mm, "mid": v(0, -67.5) * mm, "end": v(56.15, -48.18) * mm});
            skArc(sketch, "E81.16", {"start": v(-60, -40.3) * mm, "mid": v(-58.99, -44.68) * mm, "end": v(-56.15, -48.18) * mm});
            skLineSegment(sketch, "E81.17", {"start": v(-60, 40.3) * mm, "end": v(-60, -40.3) * mm});
            skArc(sketch, "E81.18", {"start": v(-56.15, 48.18) * mm, "mid": v(-58.99, 44.68) * mm, "end": v(-60, 40.3) * mm});
            skPoint(sketch, "E81.19", {"position": v(77.07, -87.07) * mm});
            skPoint(sketch, "E81.20", {"position": v(58.99, 44.68) * mm});
            skCircle(sketch, "E82", {"center": v(0, 120) * mm, "radius": 6 * mm});
            skLineSegment(sketch, "E83", {"start": v(0, 90) * mm, "end": v(0, 120) * mm, "construction": true});
            skArc(sketch, "E84.0", {"start": v(70, -90) * mm, "mid": v(77.07, -87.07) * mm, "end": v(80, -80) * mm});
            skArc(sketch, "E85", {"start": v(15, 120) * mm, "mid": v(0, 135) * mm, "end": v(-15, 120) * mm});
            skLineSegment(sketch, "E86", {"start": v(-15, 120) * mm, "end": v(-15, 108) * mm});
            skLineSegment(sketch, "E87", {"start": v(-15, 108) * mm, "end": v(-33, 90) * mm});
            skLineSegment(sketch, "E88.MirrorCS", {"start": v(15, 108) * mm, "end": v(33, 90) * mm});
            skLineSegment(sketch, "E89.MirrorCS", {"start": v(15, 120) * mm, "end": v(15, 108) * mm});
            skLineSegment(sketch, "E90", {"start": v(-80, 0) * mm, "end": v(80, 0) * mm, "construction": true});
            skLineSegment(sketch, "E91.MirrorCS", {"start": v(-15, -108) * mm, "end": v(-33, -90) * mm});
            skLineSegment(sketch, "E92.MirrorCS", {"start": v(-15, -120) * mm, "end": v(-15, -108) * mm});
            skArc(sketch, "E93.MirrorCS", {"start": v(15, -120) * mm, "mid": v(0, -135) * mm, "end": v(-15, -120) * mm});
            skLineSegment(sketch, "E94.MirrorCS", {"start": v(15, -120) * mm, "end": v(15, -108) * mm});
            skLineSegment(sketch, "E95.MirrorCS", {"start": v(15, -108) * mm, "end": v(33, -90) * mm});
            skCircle(sketch, "E96.MirrorC", {"center": v(0, -120) * mm, "radius": 6 * mm});
            skSolve(sketch);
        }
        {
            var Q0;
            Q0=makeQuery(id+"F16.imprint","IMPRINT",FACE,{"disambiguationData":[TD([[makeQuery(id+"F16.imprint","IMPRINT",EDGE,{"derivedFrom":sQuery(id+"F16.wireOp",EDGE,"E82")}),-1.0]])]});
            var Q1;
            {var subQ0=sQuery(id+"F16.wireOp",EDGE,"E91.MirrorCS");Q1=makeQuery(id+"F16.imprint","IMPRINT",FACE,{"disambiguationData":[TD([[makeQuery(id+"F16.imprint","IMPRINT",EDGE,{"derivedFrom":subQ0}),-1.0]])]});}
            var Q2;
            {var subQ7=sQuery(id+"F16.wireOp",EDGE,"E79.0");Q2=makeQuery(id+"F16.imprint","IMPRINT",FACE,{"disambiguationData":[TD([[makeQuery(id+"F16.imprint","IMPRINT",EDGE,{"derivedFrom":subQ7}),1.0]])]});}
            var Q3;
            Q3=makeQuery(id+"F2.opExtrude","CAP_FACE",FACE,{"disambiguationData":[OSD([sQuery(id+"F0.wireOp",EDGE,"E12"),sQuery(id+"F0.wireOp",EDGE,"E13"),sQuery(id+"F0.wireOp",EDGE,"E14"),sQuery(id+"F0.wireOp",EDGE,"E15"),sQuery(id+"F0.wireOp",EDGE,"E17.filletArc"),sQuery(id+"F0.wireOp",EDGE,"E18.filletArc"),sQuery(id+"F0.wireOp",EDGE,"E19.filletArc"),sQuery(id+"F0.wireOp",EDGE,"E20.filletArc"),sQuery(id+"F0.wireOp",EDGE,"E25.0"),sQuery(id+"F0.wireOp",EDGE,"E25.1"),sQuery(id+"F0.wireOp",EDGE,"E25.2"),sQuery(id+"F0.wireOp",EDGE,"E25.3"),sQuery(id+"F0.wireOp",EDGE,"E25.4"),sQuery(id+"F0.wireOp",EDGE,"E25.5"),sQuery(id+"F0.wireOp",EDGE,"E25.6"),sQuery(id+"F0.wireOp",EDGE,"E25.7")])],"isStart":false});
            extrude(context, id + "F17", {"entities" : qUnion([Q0, Q1, Q2]), "endBound" : BoundingType.UP_TO_SURFACE, "endBoundEntityFace" : qUnion([Q3]), "depth" : 25 * mm});
        }
    });
